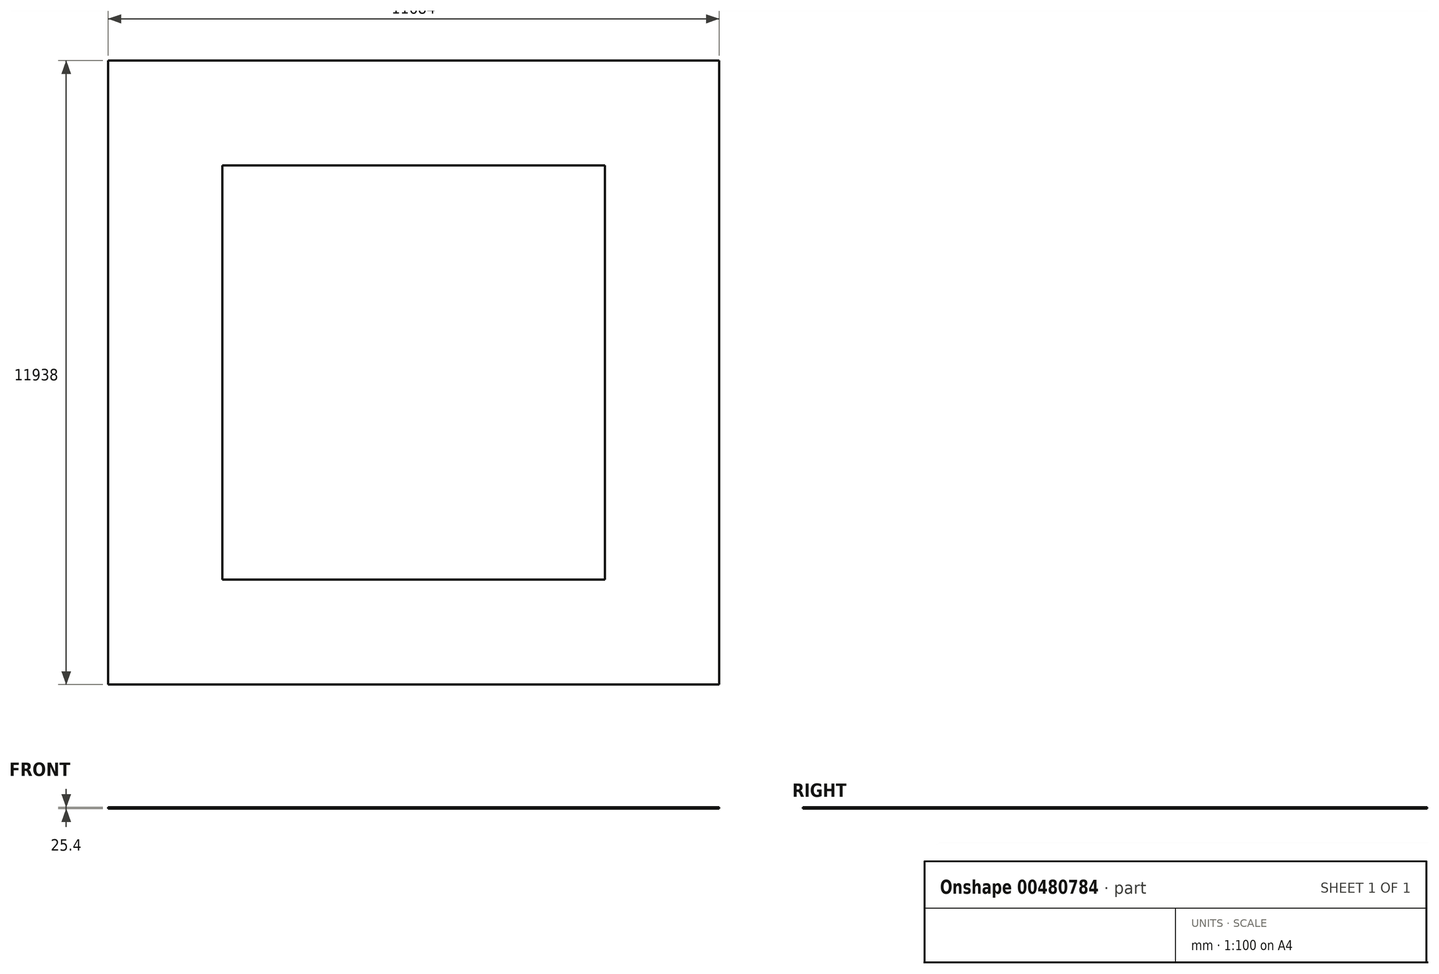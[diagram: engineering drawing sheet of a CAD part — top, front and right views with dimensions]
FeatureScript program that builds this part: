
annotation { "Feature Type Name" : "Feature", "Feature Type Description" : "" }
export const myFeature = defineFeature(function(context is Context, id is Id, definition is map)
    precondition{}
    {
        {
            var Q0;
            Q0=qCreatedBy(makeId("Top.planeOp"),FACE);
            var sketch = newSketch(context, id + "F0", { "sketchPlane" : qUnion([Q0])});
            skLineSegment(sketch, "E0.bottom", {"start": v(3657.6, -3962.4) * mm, "end": v(-3657.6, -3962.4) * mm});
            skLineSegment(sketch, "E0.top", {"start": v(3657.6, 3962.4) * mm, "end": v(-3657.6, 3962.4) * mm});
            skLineSegment(sketch, "E0.left", {"start": v(3657.6, -3962.4) * mm, "end": v(3657.6, 3962.4) * mm});
            skLineSegment(sketch, "E0.right", {"start": v(-3657.6, -3962.4) * mm, "end": v(-3657.6, 3962.4) * mm});
            skPoint(sketch, "E0.middle", {"position": v(0, 0) * mm});
            skLineSegment(sketch, "E1.bottom", {"start": v(5842, -5969) * mm, "end": v(-5842, -5969) * mm});
            skLineSegment(sketch, "E1.top", {"start": v(5842, 5969) * mm, "end": v(-5842, 5969) * mm});
            skLineSegment(sketch, "E1.left", {"start": v(5842, -5969) * mm, "end": v(5842, 5969) * mm});
            skLineSegment(sketch, "E1.right", {"start": v(-5842, -5969) * mm, "end": v(-5842, 5969) * mm});
            skSolve(sketch);
        }
        {
            var Q0;
            Q0 = qSketchRegion(id + "F0", true);
            extrude(context, id + "F1", {"entities" : qUnion([Q0]), "depth" : 25.4 * mm});
        }
    });
